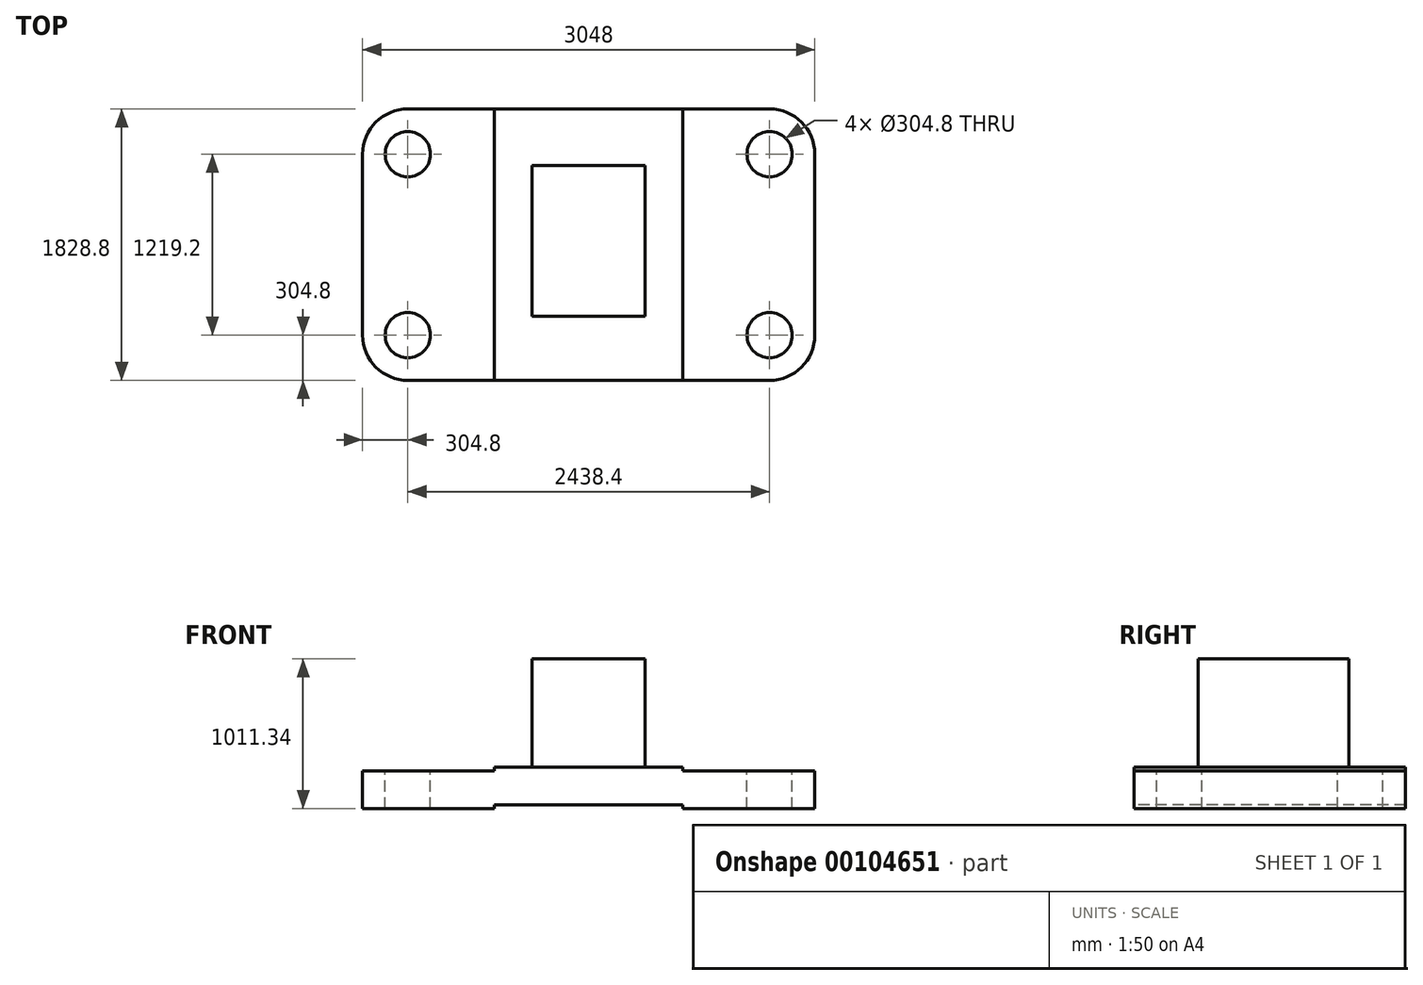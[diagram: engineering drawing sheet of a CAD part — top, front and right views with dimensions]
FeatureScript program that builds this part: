
annotation { "Feature Type Name" : "Feature", "Feature Type Description" : "" }
export const myFeature = defineFeature(function(context is Context, id is Id, definition is map)
    precondition{}
    {
        {
            var Q0;
            Q0=qCreatedBy(makeId("Top.planeOp"),FACE);
            var sketch = newSketch(context, id + "F0", { "sketchPlane" : qUnion([Q0])});
            skLineSegment(sketch, "E0.bottom", {"start": v(1524, -914.4) * mm, "end": v(-1524, -914.4) * mm});
            skLineSegment(sketch, "E0.top", {"start": v(1524, 914.4) * mm, "end": v(-1524, 914.4) * mm});
            skLineSegment(sketch, "E0.left", {"start": v(1524, -914.4) * mm, "end": v(1524, 914.4) * mm});
            skLineSegment(sketch, "E0.right", {"start": v(-1524, -914.4) * mm, "end": v(-1524, 914.4) * mm});
            skPoint(sketch, "E0.middle", {"position": v(0, 0) * mm});
            skSolve(sketch);
        }
        {
            var Q0;
            Q0=makeQuery(id+"F0.imprint","IMPRINT",FACE,{"disambiguationData":[TD([[makeQuery(id+"F0.imprint","IMPRINT",EDGE,{"derivedFrom":sQuery(id+"F0.wireOp",EDGE,"E0.bottom")}),-1.0]])]});
            extrude(context, id + "F1", {"entities" : qUnion([Q0]), "depth" : 254 * mm});
        }
        {
            var Q0;
            Q0=makeQuery(id+"F1.opExtrude","CAP_FACE",FACE,{"disambiguationData":[OSD([sQuery(id+"F0.wireOp",EDGE,"E0.bottom"),sQuery(id+"F0.wireOp",EDGE,"E0.top"),sQuery(id+"F0.wireOp",EDGE,"E0.left"),sQuery(id+"F0.wireOp",EDGE,"E0.right")])],"isStart":false});
            var sketch = newSketch(context, id + "F2", { "sketchPlane" : qUnion([Q0])});
            skLineSegment(sketch, "E1.bottom", {"start": v(-635, -914.4) * mm, "end": v(635, -914.4) * mm});
            skLineSegment(sketch, "E1.top", {"start": v(-635, 914.4) * mm, "end": v(635, 914.4) * mm});
            skLineSegment(sketch, "E1.left", {"start": v(-635, -914.4) * mm, "end": v(-635, 914.4) * mm});
            skLineSegment(sketch, "E1.right", {"start": v(635, -914.4) * mm, "end": v(635, 914.4) * mm});
            skPoint(sketch, "E1.middle", {"position": v(0, 0) * mm});
            skSolve(sketch);
        }
        {
            var Q0;
            Q0=makeQuery(id+"F2.imprint","IMPRINT",FACE,{"disambiguationData":[TD([[makeQuery(id+"F2.imprint","IMPRINT",EDGE,{"derivedFrom":sQuery(id+"F2.wireOp",EDGE,"E1.bottom")}),-1.0]])]});
            extrude(context, id + "F3", {"entities" : qUnion([Q0]), "operationType" : NewBodyOperationType.ADD, "depth" : 25.4 * mm});
        }
        {
            var Q0;
            Q0=makeQuery(id+"F1.opExtrude","CAP_FACE",FACE,{"disambiguationData":[OSD([sQuery(id+"F0.wireOp",EDGE,"E0.bottom"),sQuery(id+"F0.wireOp",EDGE,"E0.top"),sQuery(id+"F0.wireOp",EDGE,"E0.left"),sQuery(id+"F0.wireOp",EDGE,"E0.right")])],"isStart":true});
            var sketch = newSketch(context, id + "F4", { "sketchPlane" : qUnion([Q0])});
            skLineSegment(sketch, "E2.0.0", {"start": v(-635, -914.4) * mm, "end": v(-635, 914.4) * mm});
            skLineSegment(sketch, "E2.0.1", {"start": v(-635, 914.4) * mm, "end": v(635, 914.4) * mm});
            skLineSegment(sketch, "E2.0.2", {"start": v(635, 914.4) * mm, "end": v(635, -914.4) * mm});
            skLineSegment(sketch, "E2.0.3", {"start": v(635, -914.4) * mm, "end": v(-635, -914.4) * mm});
            skSolve(sketch);
        }
        {
            var Q0;
            Q0 = qSketchRegion(id + "F4", true);
            extrude(context, id + "F5", {"entities" : qUnion([Q0]), "operationType" : NewBodyOperationType.REMOVE, "oppositeDirection" : true, "depth" : 25.4 * mm});
        }
        {
            var Q0;
            Q0=makeQuery(id+"F1.opExtrude","SWEPT_EDGE",EDGE,{"disambiguationData":[OSD([sQuery(id+"F0.wireOp",EDGE,"E0.bottom"),sQuery(id+"F0.wireOp",EDGE,"E0.left")])]});
            var Q1;
            Q1=makeQuery(id+"F1.opExtrude","SWEPT_EDGE",EDGE,{"disambiguationData":[OSD([sQuery(id+"F0.wireOp",EDGE,"E0.top"),sQuery(id+"F0.wireOp",EDGE,"E0.left")])]});
            var Q2;
            Q2=makeQuery(id+"F1.opExtrude","SWEPT_EDGE",EDGE,{"disambiguationData":[OSD([sQuery(id+"F0.wireOp",EDGE,"E0.bottom"),sQuery(id+"F0.wireOp",EDGE,"E0.right")])]});
            var Q3;
            Q3=makeQuery(id+"F1.opExtrude","SWEPT_EDGE",EDGE,{"disambiguationData":[OSD([sQuery(id+"F0.wireOp",EDGE,"E0.top"),sQuery(id+"F0.wireOp",EDGE,"E0.right")])]});
            fillet(context, id + "F6", {"entities" : qUnion([Q0, Q1, Q2, Q3]), "radius" : 304.8 * mm, "tangentPropagation" : true, "allowEdgeOverflow" : false});
        }
        {
            var Q0;
            {var subQ0=sQuery(id+"F0.wireOp",EDGE,"E0.right");var subQ1=sQuery(id+"F0.wireOp",EDGE,"E0.top");var subQ2=sQuery(id+"F0.wireOp",EDGE,"E0.bottom");Q0=makeQuery(id+"F3.boolean.opBoolean","SPLIT",FACE,{"disambiguationData":[TD([makeQuery(id+"F1.opExtrude","SWEPT_FACE",FACE,{"disambiguationData":[OSD([subQ0])]})])],"derivedFrom":makeQuery(id+"F1.opExtrude","CAP_FACE",FACE,{"disambiguationData":[OSD([subQ2,subQ1,sQuery(id+"F0.wireOp",EDGE,"E0.left"),subQ0])],"isStart":false})});}
            var sketch = newSketch(context, id + "F7", { "sketchPlane" : qUnion([Q0])});
            skPoint(sketch, "E3", {"position": v(-1219.2, 609.6) * mm});
            skPoint(sketch, "E4", {"position": v(-1219.2, -609.6) * mm});
            skSolve(sketch);
        }
        {
            var Q0;
            {var subQ0=sQuery(id+"F0.wireOp",EDGE,"E0.left");var subQ1=sQuery(id+"F0.wireOp",EDGE,"E0.top");var subQ2=sQuery(id+"F0.wireOp",EDGE,"E0.bottom");Q0=makeQuery(id+"F3.boolean.opBoolean","SPLIT",FACE,{"disambiguationData":[TD([makeQuery(id+"F1.opExtrude","SWEPT_FACE",FACE,{"disambiguationData":[OSD([subQ0])]})])],"derivedFrom":makeQuery(id+"F1.opExtrude","CAP_FACE",FACE,{"disambiguationData":[OSD([subQ2,subQ1,subQ0,sQuery(id+"F0.wireOp",EDGE,"E0.right")])],"isStart":false})});}
            var sketch = newSketch(context, id + "F8", { "sketchPlane" : qUnion([Q0])});
            skPoint(sketch, "E5", {"position": v(1219.2, 609.6) * mm});
            skPoint(sketch, "E6", {"position": v(1219.2, -609.6) * mm});
            skSolve(sketch);
        }
        {
            var Q0;
            Q0=sQuery(id+"F7.wireOp",VERTEX,"E3");
            var Q1;
            Q1=sQuery(id+"F7.wireOp",VERTEX,"E4");
            var Q2;
            Q2=sQuery(id+"F8.wireOp",VERTEX,"E5");
            var Q3;
            Q3=sQuery(id+"F8.wireOp",VERTEX,"E6");
            var Q4;
            Q4=makeQuery(id+"F1.opExtrude","SWEPT_BODY",BODY,{"disambiguationData":[OSD([sQuery(id+"F0.wireOp",EDGE,"E0.bottom"),sQuery(id+"F0.wireOp",EDGE,"E0.top"),sQuery(id+"F0.wireOp",EDGE,"E0.left"),sQuery(id+"F0.wireOp",EDGE,"E0.right")])]});
            hole(context, id + "F9", {"style" : HoleStyle.SIMPLE, "endStyle" : HoleEndStyle.THROUGH, "holeDiameter" : 304.8 * mm, "locations" : qUnion([Q0, Q1, Q2, Q3]), "scope" : qUnion([Q4]), "isTappedThrough" : true});
        }
        {
            var Q0;
            Q0=makeQuery(id+"F3.opExtrude","CAP_FACE",FACE,{"disambiguationData":[OSD([sQuery(id+"F2.wireOp",EDGE,"E1.bottom"),sQuery(id+"F2.wireOp",EDGE,"E1.top"),sQuery(id+"F2.wireOp",EDGE,"E1.left"),sQuery(id+"F2.wireOp",EDGE,"E1.right")])],"isStart":false});
            var sketch = newSketch(context, id + "F10", { "sketchPlane" : qUnion([Q0])});
            skLineSegment(sketch, "E7.bottom", {"start": v(-381, 533.4) * mm, "end": v(381, 533.4) * mm});
            skLineSegment(sketch, "E7.top", {"start": v(-381, -482.6) * mm, "end": v(381, -482.6) * mm});
            skLineSegment(sketch, "E7.left", {"start": v(-381, 533.4) * mm, "end": v(-381, -482.6) * mm});
            skLineSegment(sketch, "E7.right", {"start": v(381, 533.4) * mm, "end": v(381, -482.6) * mm});
            skSolve(sketch);
        }
        {
            var Q0;
            Q0=makeQuery(id+"F10.imprint","IMPRINT",FACE,{"disambiguationData":[TD([[makeQuery(id+"F10.imprint","IMPRINT",EDGE,{"derivedFrom":sQuery(id+"F10.wireOp",EDGE,"E7.bottom")}),-1.0]])]});
            var Q1;
            Q1=sQuery(id+"F10.wireOp",EDGE,"E7.bottom");
            var Q2;
            Q2=sQuery(id+"F10.wireOp",EDGE,"E7.right");
            var Q3;
            Q3=sQuery(id+"F10.wireOp",EDGE,"E7.top");
            extrude(context, id + "F11", {"entities" : qUnion([Q0]), "surfaceEntities" : qUnion([Q1, Q2, Q3]), "depth" : 731.94 * mm});
        }
    });
